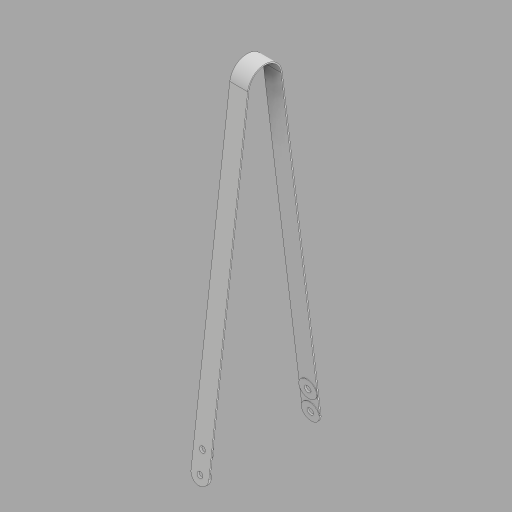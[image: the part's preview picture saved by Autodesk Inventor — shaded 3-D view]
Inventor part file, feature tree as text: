
AUTODESK INVENTOR PART (.ipt)
format: ipt  version: 2023 (Build 270158000, 158)  size: 161,792 bytes
history: native  units: mm
features: extrude x7, sketch x3
ambient origin geometry x8: Origin, YZ Plane, XZ Plane, XY Plane, X Axis, Y Axis, Z Axis, Center Point
bodies: Solid1 (feature_tree)
feature tree (10):
  extrude  "Extrusion1"  Depth=254.37mm
  sketch  "Sketch2"  dims[d2=180.0deg d3=35.0mm]
  extrude  "Extrusion2"  Depth=35.0mm
  extrude  "Extrusion3"  Depth=0.5mm
  extrude  "Extrusion4"  Depth=1.0mm
  sketch  "Sketch3"  dims[d4=100.0mm d5=2.0mm d6=1.0mm d7=1.0mm d8=15.0mm d9=0.0mm d10=15.0mm d11=15.0mm d12=2.5mm d13=15.0mm d14=15.0mm d15=1.0mm d16=0.0mm d17=2.0mm d18=0.0mm d19=2.0mm d20=0.0mm d21=15.0mm d22=15.0mm d23=2.5mm d24=15.0mm d25=1.0mm d26=0.0mm d27=5.5mm d29=2.0mm d30=0.0mm d31=2.0mm d32=0.0mm d33=5.5mm d34=15.0mm d35=0.872665mm d36=0.5mm d37=0.872665mm]
  extrude  "Extrusion5"  Depth=1.0mm
  extrude  "Extrusion6"  Depth=15.0mm TaperAngle=0.0deg
  extrude  "Extrusion7"  Depth=15.0mm
  sketch  "Sketch1"  dims[d0=29.224mm d1=254.37mm]
